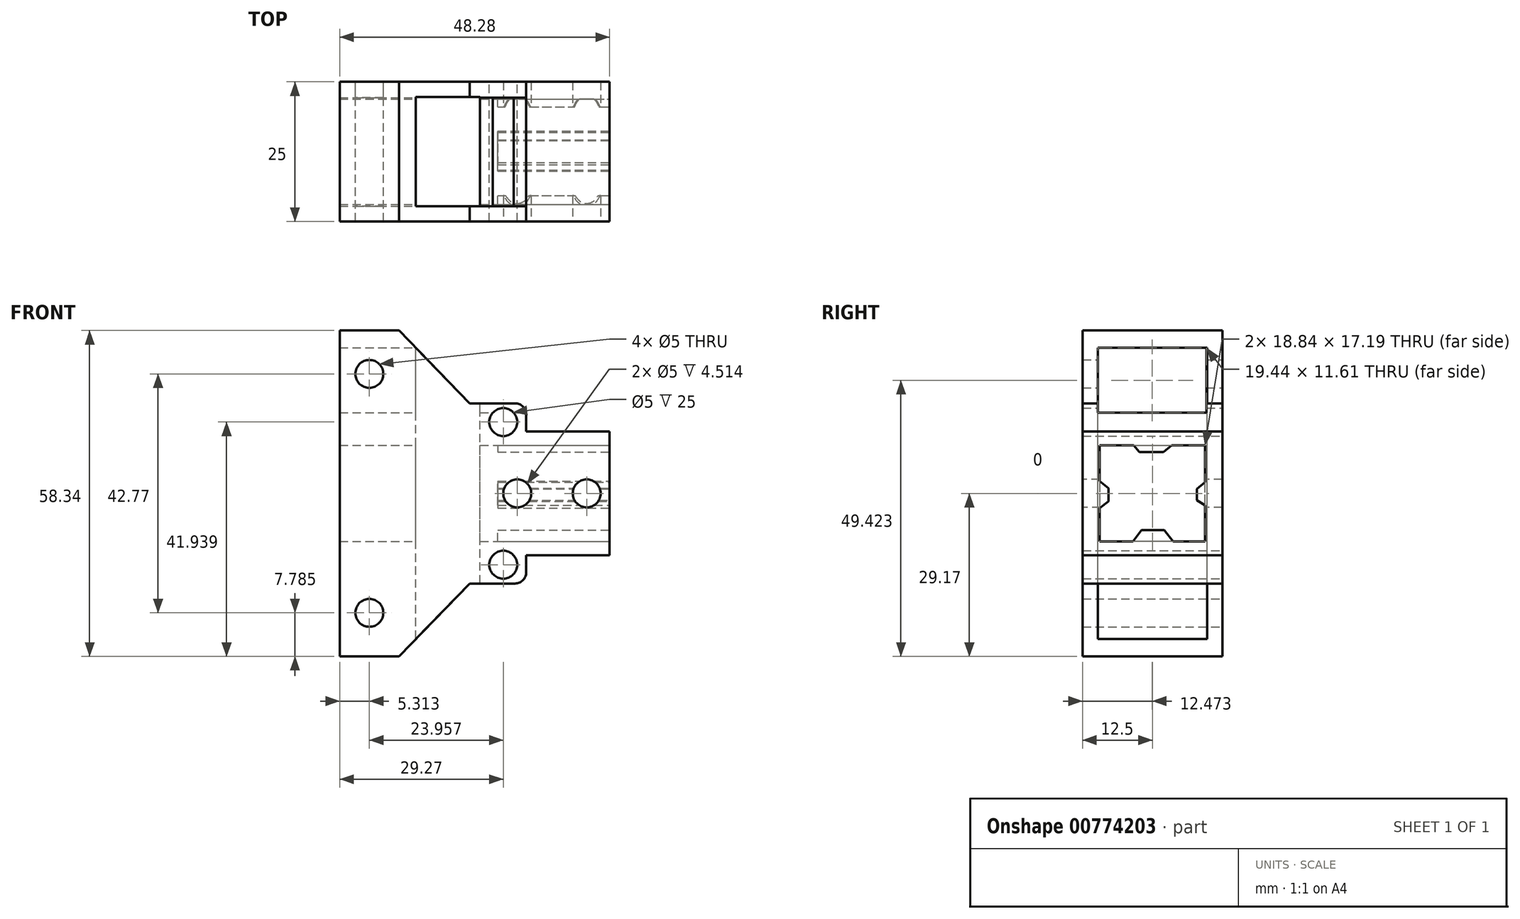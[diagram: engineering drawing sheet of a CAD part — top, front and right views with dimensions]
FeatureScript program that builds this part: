
annotation { "Feature Type Name" : "Feature", "Feature Type Description" : "" }
export const myFeature = defineFeature(function(context is Context, id is Id, definition is map)
    precondition{}
    {
        {
            var Q0;
            Q0=qCreatedBy(makeId("Front.planeOp"),FACE);
            var sketch = newSketch(context, id + "F0", { "sketchPlane" : qUnion([Q0])});
            skLineSegment(sketch, "E0", {"start": v(9.34, 11.07) * mm, "end": v(-5.57, 11.07) * mm});
            skLineSegment(sketch, "E1", {"start": v(-15.68, 16.13) * mm, "end": v(-28.3, 29.17) * mm});
            skLineSegment(sketch, "E2", {"start": v(-28.3, 29.17) * mm, "end": v(-38.94, 29.17) * mm});
            skLineSegment(sketch, "E3", {"start": v(-38.94, 29.17) * mm, "end": v(-38.94, 0) * mm});
            skLineSegment(sketch, "E4.MirrorCS", {"start": v(-15.68, -16.13) * mm, "end": v(-28.3, -29.17) * mm});
            skLineSegment(sketch, "E5.MirrorCS", {"start": v(-38.94, -29.17) * mm, "end": v(-38.94, 0) * mm});
            skLineSegment(sketch, "E6.MirrorCS", {"start": v(-28.3, -29.17) * mm, "end": v(-38.94, -29.17) * mm});
            skLineSegment(sketch, "E7.MirrorCS", {"start": v(9.34, -11.07) * mm, "end": v(-5.57, -11.07) * mm});
            skLineSegment(sketch, "E8", {"start": v(9.34, 11.07) * mm, "end": v(9.34, 0) * mm});
            skLineSegment(sketch, "E9.MirrorCS", {"start": v(9.34, -11.07) * mm, "end": v(9.34, 0) * mm});
            skLineSegment(sketch, "E10", {"start": v(-33.63, 29.17) * mm, "end": v(-33.63, 0) * mm, "construction": true});
            skCircle(sketch, "E11", {"center": v(-33.63, 21.38) * mm, "radius": 2.5 * mm});
            skCircle(sketch, "E12.MirrorC", {"center": v(-33.63, -21.38) * mm, "radius": 2.5 * mm});
            skLineSegment(sketch, "E13", {"start": v(-15.68, 16.13) * mm, "end": v(-7.57, 16.13) * mm});
            skLineSegment(sketch, "E14", {"start": v(-5.57, 14.13) * mm, "end": v(-5.57, 11.07) * mm});
            skPoint(sketch, "E15.orphan", {"position": v(-10.78, 11.07) * mm});
            skPoint(sketch, "E16.visualSharp", {"position": v(-5.57, 16.13) * mm});
            skArc(sketch, "E16.filletArc", {"start": v(-5.57, 14.13) * mm, "mid": v(-6.16, 15.55) * mm, "end": v(-7.57, 16.13) * mm});
            skArc(sketch, "E17.MirrorCS", {"start": v(-5.57, -14.13) * mm, "mid": v(-6.16, -15.55) * mm, "end": v(-7.57, -16.13) * mm});
            skPoint(sketch, "E18.MirrorP", {"position": v(-5.57, -16.13) * mm});
            skLineSegment(sketch, "E19.MirrorCS", {"start": v(-15.68, -16.13) * mm, "end": v(-7.57, -16.13) * mm});
            skLineSegment(sketch, "E20.MirrorCS", {"start": v(-5.57, -14.13) * mm, "end": v(-5.57, -11.07) * mm});
            skPoint(sketch, "E21.MirrorP", {"position": v(-10.78, -11.07) * mm});
            skCircle(sketch, "E22", {"center": v(-9.67, 12.77) * mm, "radius": 2.5 * mm});
            skCircle(sketch, "E23.MirrorC", {"center": v(-9.67, -12.77) * mm, "radius": 2.5 * mm});
            skSolve(sketch);
        }
        {
            var Q0;
            Q0 = qSketchRegion(id + "F0", true);
            extrude(context, id + "F1", {"entities" : qUnion([Q0]), "depth" : 25 * mm, "offsetDistance" : 25 * mm, "symmetric" : true});
        }
        {
            var Q0;
            Q0=makeQuery(id+"F1.opExtrude","SWEPT_FACE",FACE,{"disambiguationData":[OSD([sQuery(id+"F0.wireOp",EDGE,"E8"),sQuery(id+"F0.wireOp",EDGE,"E9.MirrorCS")])]});
            var sketch = newSketch(context, id + "F2", { "sketchPlane" : qUnion([Q0])});
            skLineSegment(sketch, "E24", {"start": v(0, 8.6) * mm, "end": v(-9.42, 8.6) * mm});
            skLineSegment(sketch, "E25", {"start": v(-9.42, 8.6) * mm, "end": v(-9.42, 0) * mm});
            skLineSegment(sketch, "E26.MirrorCS", {"start": v(0, 8.6) * mm, "end": v(9.42, 8.6) * mm});
            skLineSegment(sketch, "E27.MirrorCS", {"start": v(9.42, 8.6) * mm, "end": v(9.42, 0) * mm});
            skLineSegment(sketch, "E28.MirrorCS", {"start": v(0, -8.6) * mm, "end": v(9.42, -8.6) * mm});
            skLineSegment(sketch, "E29.MirrorCS", {"start": v(0, -8.6) * mm, "end": v(-9.42, -8.6) * mm});
            skLineSegment(sketch, "E30.MirrorCS", {"start": v(9.42, -8.6) * mm, "end": v(9.42, 0) * mm});
            skLineSegment(sketch, "E31.MirrorCS", {"start": v(-9.42, -8.6) * mm, "end": v(-9.42, 0) * mm});
            skSolve(sketch);
        }
        {
            var Q0;
            Q0 = qSketchRegion(id + "F2", true);
            extrude(context, id + "F3", {"entities" : qUnion([Q0]), "operationType" : NewBodyOperationType.REMOVE, "endBound" : BoundingType.THROUGH_ALL, "oppositeDirection" : true, "depth" : 25 * mm, "offsetDistance" : 25 * mm});
        }
        {
            var Q0;
            Q0=makeQuery(id+"F1.opExtrude","SWEPT_FACE",FACE,{"disambiguationData":[OSD([sQuery(id+"F0.wireOp",EDGE,"E8"),sQuery(id+"F0.wireOp",EDGE,"E9.MirrorCS")])]});
            var sketch = newSketch(context, id + "F4", { "sketchPlane" : qUnion([Q0])});
            skLineSegment(sketch, "E32", {"start": v(-3.32, 8.6) * mm, "end": v(-2.35, 7.39) * mm});
            skLineSegment(sketch, "E33", {"start": v(-2.35, 7.39) * mm, "end": v(2, 7.39) * mm});
            skLineSegment(sketch, "E34", {"start": v(2, 7.39) * mm, "end": v(3.46, 8.6) * mm});
            skLineSegment(sketch, "E35", {"start": v(-3.32, 8.6) * mm, "end": v(3.46, 8.6) * mm});
            skLineSegment(sketch, "E36", {"start": v(9.42, 1.98) * mm, "end": v(7.99, 0.79) * mm});
            skLineSegment(sketch, "E37", {"start": v(7.99, 0.79) * mm, "end": v(7.99, -1.24) * mm});
            skLineSegment(sketch, "E38", {"start": v(7.99, -1.24) * mm, "end": v(9.42, -2.13) * mm});
            skLineSegment(sketch, "E39", {"start": v(-3.48, -8.6) * mm, "end": v(-1.95, -6.57) * mm});
            skLineSegment(sketch, "E40", {"start": v(-1.95, -6.57) * mm, "end": v(2.08, -6.57) * mm});
            skLineSegment(sketch, "E41", {"start": v(2.08, -6.57) * mm, "end": v(3.7, -8.6) * mm});
            skLineSegment(sketch, "E42", {"start": v(-9.42, 2.22) * mm, "end": v(-7.84, 0.93) * mm});
            skLineSegment(sketch, "E43", {"start": v(-7.84, 0.93) * mm, "end": v(-7.84, -1.4) * mm});
            skLineSegment(sketch, "E44", {"start": v(-7.84, -1.4) * mm, "end": v(-9.42, -2.61) * mm});
            skLineSegment(sketch, "E45", {"start": v(-9.42, 2.22) * mm, "end": v(-9.42, -2.61) * mm});
            skLineSegment(sketch, "E46", {"start": v(9.42, 1.98) * mm, "end": v(9.42, -2.13) * mm});
            skLineSegment(sketch, "E47", {"start": v(3.7, -8.6) * mm, "end": v(-3.48, -8.6) * mm});
            skSolve(sketch);
        }
        {
            var Q0;
            Q0 = qSketchRegion(id + "F4", true);
            extrude(context, id + "F5", {"entities" : qUnion([Q0]), "operationType" : NewBodyOperationType.ADD, "oppositeDirection" : true, "depth" : 20 * mm, "offsetDistance" : 25 * mm});
        }
        {
            var Q0;
            Q0=qCreatedBy(makeId("Top.planeOp"),FACE);
            var sketch = newSketch(context, id + "F6", { "sketchPlane" : qUnion([Q0])});
            skLineSegment(sketch, "E48", {"start": v(-25.3, 9.78) * mm, "end": v(-13.8, 9.78) * mm});
            skLineSegment(sketch, "E49", {"start": v(-13.8, 9.78) * mm, "end": v(-13.8, 0) * mm});
            skLineSegment(sketch, "E50", {"start": v(-25.3, 9.78) * mm, "end": v(-25.3, 0) * mm});
            skLineSegment(sketch, "E51.MirrorCS", {"start": v(-25.3, -9.78) * mm, "end": v(-25.3, 0) * mm});
            skLineSegment(sketch, "E52.MirrorCS", {"start": v(-25.3, -9.78) * mm, "end": v(-13.8, -9.78) * mm});
            skLineSegment(sketch, "E53.MirrorCS", {"start": v(-13.8, -9.78) * mm, "end": v(-13.8, 0) * mm});
            skSolve(sketch);
        }
        {
            var Q0;
            Q0 = qSketchRegion(id + "F6", true);
            extrude(context, id + "F7", {"entities" : qUnion([Q0]), "operationType" : NewBodyOperationType.REMOVE, "oppositeDirection" : true, "depth" : 100 * mm, "offsetDistance" : 25 * mm, "symmetric" : true});
        }
        {
            var Q0;
            Q0=qCreatedBy(makeId("Right.planeOp"),FACE);
            var sketch = newSketch(context, id + "F8", { "sketchPlane" : qUnion([Q0])});
            skLineSegment(sketch, "E54", {"start": v(-9.75, 26.06) * mm, "end": v(9.7, 26.06) * mm});
            skLineSegment(sketch, "E55", {"start": v(9.7, 26.06) * mm, "end": v(9.7, 14.45) * mm});
            skLineSegment(sketch, "E56", {"start": v(9.7, 14.45) * mm, "end": v(-9.75, 14.45) * mm});
            skLineSegment(sketch, "E57", {"start": v(-9.75, 14.45) * mm, "end": v(-9.75, 26.06) * mm});
            skSolve(sketch);
        }
        {
            var Q0;
            Q0 = qSketchRegion(id + "F8", true);
            extrude(context, id + "F9", {"entities" : qUnion([Q0]), "operationType" : NewBodyOperationType.REMOVE, "endBound" : BoundingType.THROUGH_ALL, "oppositeDirection" : true, "depth" : 25 * mm, "offsetDistance" : 25 * mm});
        }
        {
            var Q0;
            Q0=makeQuery(id+"F1.opExtrude","CAP_FACE",FACE,{"disambiguationData":[OSD([sQuery(id+"F0.wireOp",EDGE,"E0"),sQuery(id+"F0.wireOp",EDGE,"E1"),sQuery(id+"F0.wireOp",EDGE,"E2"),sQuery(id+"F0.wireOp",EDGE,"E3"),sQuery(id+"F0.wireOp",EDGE,"E4.MirrorCS"),sQuery(id+"F0.wireOp",EDGE,"E5.MirrorCS"),sQuery(id+"F0.wireOp",EDGE,"E6.MirrorCS"),sQuery(id+"F0.wireOp",EDGE,"E7.MirrorCS"),sQuery(id+"F0.wireOp",EDGE,"E8"),sQuery(id+"F0.wireOp",EDGE,"E9.MirrorCS"),sQuery(id+"F0.wireOp",EDGE,"E11"),sQuery(id+"F0.wireOp",EDGE,"E12.MirrorC")])],"isStart":false});
            var sketch = newSketch(context, id + "F10", { "sketchPlane" : qUnion([Q0])});
            skCircle(sketch, "E58", {"center": v(-7.17, 0) * mm, "radius": 2.5 * mm});
            skCircle(sketch, "E59", {"center": v(5.26, 0) * mm, "radius": 2.5 * mm});
            skSolve(sketch);
        }
        {
            var Q0;
            Q0 = qSketchRegion(id + "F10", true);
            extrude(context, id + "F11", {"entities" : qUnion([Q0]), "operationType" : NewBodyOperationType.REMOVE, "endBound" : BoundingType.THROUGH_ALL, "oppositeDirection" : true, "depth" : 25 * mm, "offsetDistance" : 25 * mm});
        }
    });
